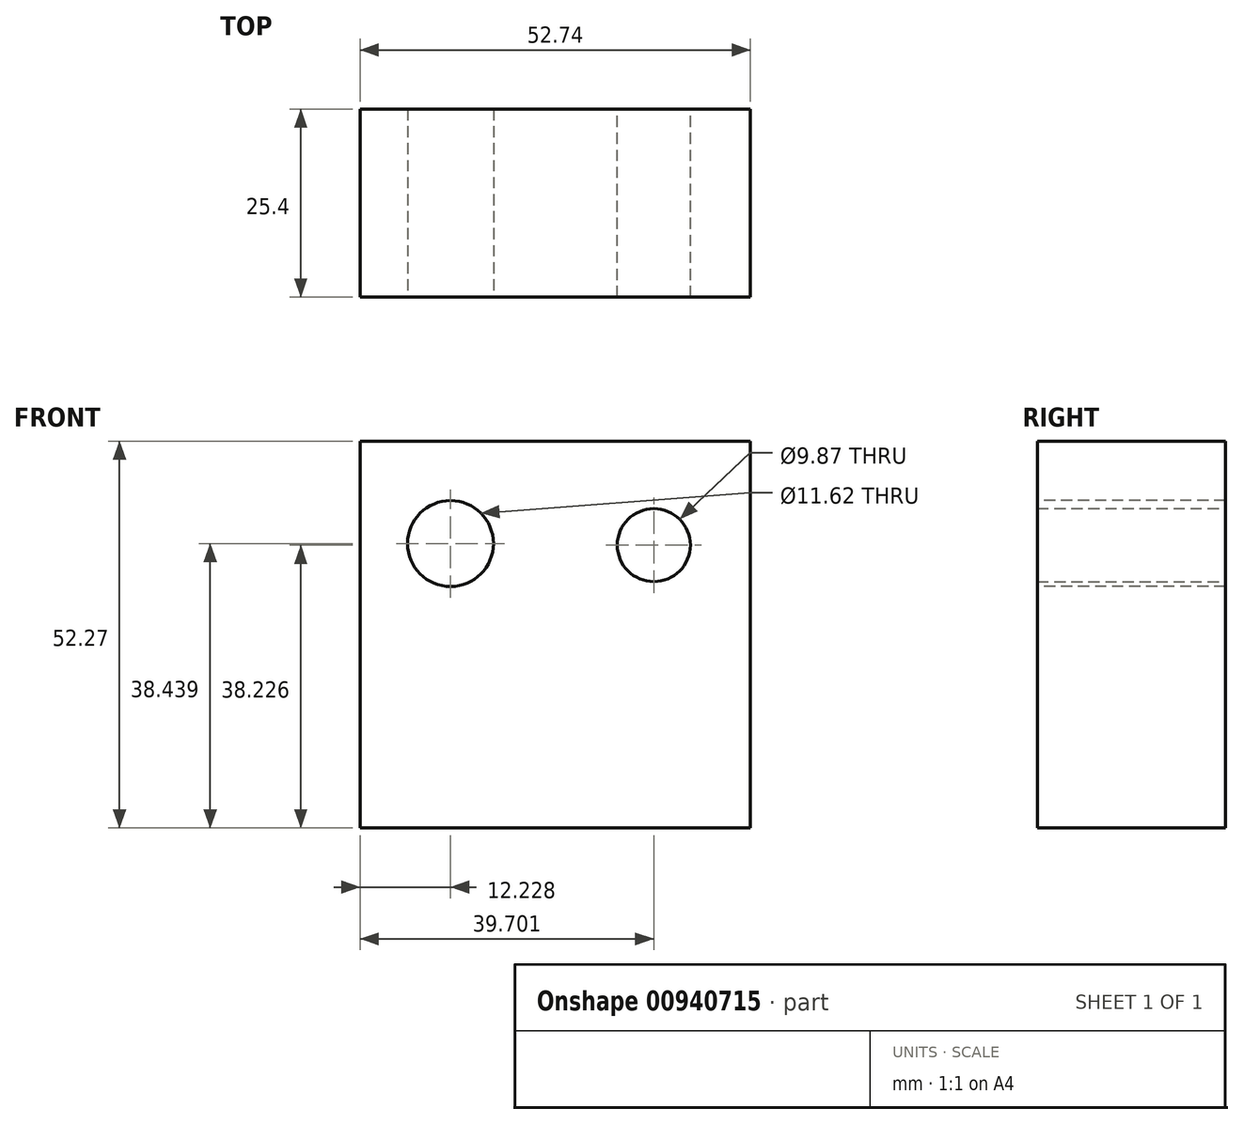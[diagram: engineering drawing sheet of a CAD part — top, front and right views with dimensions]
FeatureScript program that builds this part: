
annotation { "Feature Type Name" : "Feature", "Feature Type Description" : "" }
export const myFeature = defineFeature(function(context is Context, id is Id, definition is map)
    precondition{}
    {
        {
            var Q0;
            Q0=qCreatedBy(makeId("Front.planeOp"),FACE);
            var sketch = newSketch(context, id + "F0", { "sketchPlane" : qUnion([Q0])});
            skLineSegment(sketch, "E0.bottom", {"start": v(-27.47, 28.98) * mm, "end": v(25.27, 28.98) * mm});
            skLineSegment(sketch, "E0.top", {"start": v(-27.47, -23.3) * mm, "end": v(25.27, -23.3) * mm});
            skLineSegment(sketch, "E0.left", {"start": v(-27.47, 28.98) * mm, "end": v(-27.47, -23.3) * mm});
            skLineSegment(sketch, "E0.right", {"start": v(25.27, 28.98) * mm, "end": v(25.27, -23.3) * mm});
            skSolve(sketch);
        }
        {
            var Q0;
            Q0 = qSketchRegion(id + "F0", true);
            extrude(context, id + "F1", {"entities" : qUnion([Q0]), "depth" : 25.4 * mm, "offsetDistance" : 25.4 * mm});
        }
        {
            var Q0;
            Q0=qCreatedBy(makeId("Front.planeOp"),FACE);
            var sketch = newSketch(context, id + "F2", { "sketchPlane" : qUnion([Q0])});
            skCircle(sketch, "E1", {"center": v(-12.82, 11.4) * mm, "radius": 4.81 * mm});
            skSolve(sketch);
        }
        {
            var Q0;
            Q0 = qSketchRegion(id + "F2", true);
            extrude(context, id + "F3", {"entities" : qUnion([Q0]), "operationType" : NewBodyOperationType.REMOVE, "oppositeDirection" : true, "depth" : 126.1 * mm, "offsetDistance" : 25.4 * mm});
        }
        {
            var Q0;
            Q0=makeQuery(id+"F1.opExtrude","CAP_FACE",FACE,{"disambiguationData":[OSD([sQuery(id+"F0.wireOp",EDGE,"E0.bottom"),sQuery(id+"F0.wireOp",EDGE,"E0.top"),sQuery(id+"F0.wireOp",EDGE,"E0.left"),sQuery(id+"F0.wireOp",EDGE,"E0.right")])],"isStart":true});
            var sketch = newSketch(context, id + "F4", { "sketchPlane" : qUnion([Q0])});
            skCircle(sketch, "E2", {"center": v(-12.23, 14.94) * mm, "radius": 4.94 * mm});
            skSolve(sketch);
        }
        {
            var Q0;
            Q0=makeQuery(id+"F4.imprint","IMPRINT",FACE,{"disambiguationData":[TD([[makeQuery(id+"F4.imprint","IMPRINT",EDGE,{"derivedFrom":sQuery(id+"F4.wireOp",EDGE,"E2")}),1.0]])]});
            var Q1;
            Q1=sQuery(id+"F4.wireOp",EDGE,"E2");
            extrude(context, id + "F5", {"entities" : qUnion([Q0]), "operationType" : NewBodyOperationType.REMOVE, "surfaceEntities" : qUnion([Q1]), "oppositeDirection" : true, "depth" : 76.2 * mm, "offsetDistance" : 25.4 * mm});
        }
        {
            var Q0;
            Q0=makeQuery(id+"F1.opExtrude","CAP_FACE",FACE,{"disambiguationData":[OSD([sQuery(id+"F0.wireOp",EDGE,"E0.bottom"),sQuery(id+"F0.wireOp",EDGE,"E0.top"),sQuery(id+"F0.wireOp",EDGE,"E0.left"),sQuery(id+"F0.wireOp",EDGE,"E0.right")])],"isStart":false});
            var sketch = newSketch(context, id + "F6", { "sketchPlane" : qUnion([Q0])});
            skCircle(sketch, "E3", {"center": v(-15.24, 15.15) * mm, "radius": 5.8 * mm});
            skSolve(sketch);
        }
        {
            var Q0;
            Q0=sQuery(id+"F6.wireOp",EDGE,"E3");
            extrude(context, id + "F7", {"bodyType" : ToolBodyType.SURFACE, "surfaceEntities" : qUnion([Q0]), "oppositeDirection" : true, "depth" : 27.79 * mm, "offsetDistance" : 25.4 * mm});
        }
        {
            var Q0;
            Q0 = qSketchRegion(id + "F6", true);
            extrude(context, id + "F8", {"entities" : qUnion([Q0]), "operationType" : NewBodyOperationType.REMOVE, "oppositeDirection" : true, "depth" : 25.4 * mm, "offsetDistance" : 25.4 * mm});
        }
    });
